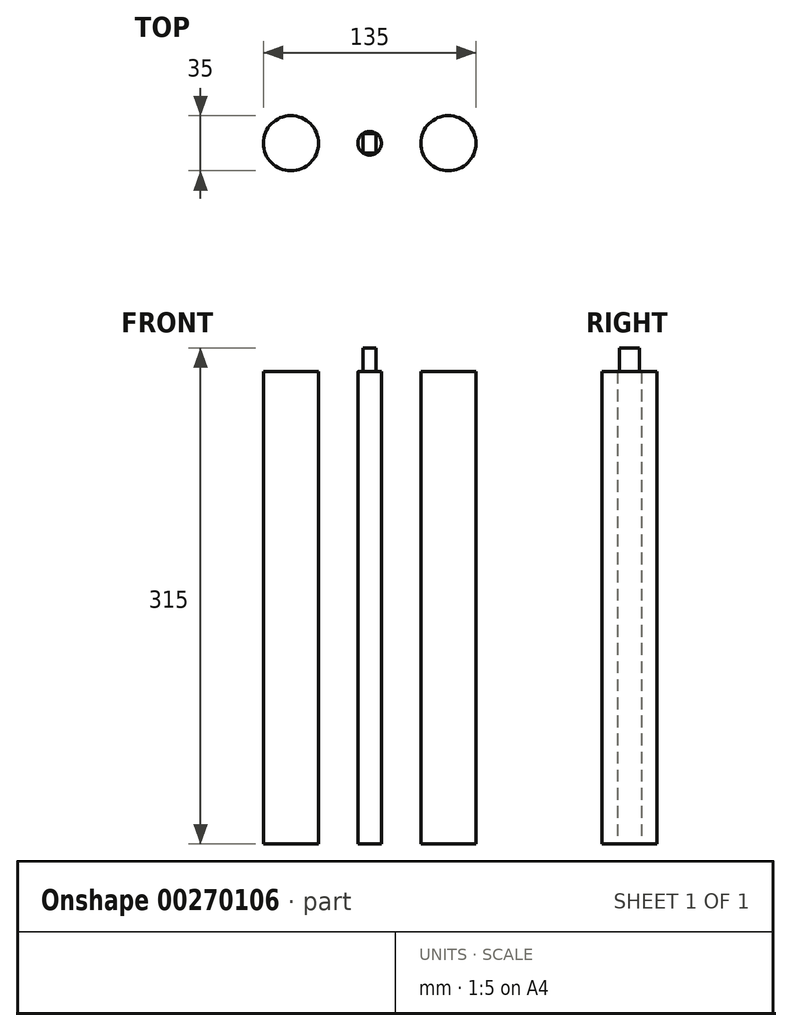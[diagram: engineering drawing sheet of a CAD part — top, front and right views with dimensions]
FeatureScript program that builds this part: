
annotation { "Feature Type Name" : "Feature", "Feature Type Description" : "" }
export const myFeature = defineFeature(function(context is Context, id is Id, definition is map)
    precondition{}
    {
        {
            var Q0;
            Q0=qCreatedBy(makeId("Top.planeOp"),FACE);
            var sketch = newSketch(context, id + "F0", { "sketchPlane" : qUnion([Q0])});
            skPoint(sketch, "E0", {"position": v(-50, 0) * mm});
            skPoint(sketch, "E1", {"position": v(50, 0) * mm});
            skCircle(sketch, "E2", {"center": v(-50, 0) * mm, "radius": 17.5 * mm});
            skCircle(sketch, "E3", {"center": v(50, 0) * mm, "radius": 17.5 * mm});
            skCircle(sketch, "E4", {"center": v(0, 0) * mm, "radius": 7.5 * mm});
            skSolve(sketch);
        }
        {
            var Q0;
            Q0=makeQuery(id+"F0.imprint","IMPRINT",FACE,{"disambiguationData":[TD([[makeQuery(id+"F0.imprint","IMPRINT",EDGE,{"derivedFrom":sQuery(id+"F0.wireOp",EDGE,"E2")}),1.0]])]});
            var Q1;
            Q1=makeQuery(id+"F0.imprint","IMPRINT",FACE,{"disambiguationData":[TD([[makeQuery(id+"F0.imprint","IMPRINT",EDGE,{"derivedFrom":sQuery(id+"F0.wireOp",EDGE,"E4")}),1.0]])]});
            var Q2;
            Q2=makeQuery(id+"F0.imprint","IMPRINT",FACE,{"disambiguationData":[TD([[makeQuery(id+"F0.imprint","IMPRINT",EDGE,{"derivedFrom":sQuery(id+"F0.wireOp",EDGE,"E3")}),1.0]])]});
            extrude(context, id + "F1", {"entities" : qUnion([Q0, Q1, Q2]), "depth" : 300 * mm});
        }
        {
            var Q0;
            Q0=makeQuery(id+"F1.opExtrude","CAP_FACE",FACE,{"disambiguationData":[OSD([sQuery(id+"F0.wireOp",EDGE,"E4")])],"isStart":false});
            var sketch = newSketch(context, id + "F2", { "sketchPlane" : qUnion([Q0])});
            skLineSegment(sketch, "E5.bottom", {"start": v(4.12, -6.27) * mm, "end": v(-4.12, -6.27) * mm});
            skLineSegment(sketch, "E5.top", {"start": v(4.12, 6.27) * mm, "end": v(-4.12, 6.27) * mm});
            skLineSegment(sketch, "E5.left", {"start": v(4.12, -6.27) * mm, "end": v(4.12, 6.27) * mm});
            skLineSegment(sketch, "E5.right", {"start": v(-4.12, -6.27) * mm, "end": v(-4.12, 6.27) * mm});
            skPoint(sketch, "E5.middle", {"position": v(0, 0) * mm});
            skSolve(sketch);
        }
        {
            var Q0;
            Q0=makeQuery(id+"F2.imprint","IMPRINT",FACE,{"disambiguationData":[TD([[makeQuery(id+"F2.imprint","IMPRINT",EDGE,{"derivedFrom":sQuery(id+"F2.wireOp",EDGE,"E5.bottom")}),-1.0]])]});
            extrude(context, id + "F3", {"entities" : qUnion([Q0]), "operationType" : NewBodyOperationType.ADD, "depth" : 15 * mm});
        }
    });
